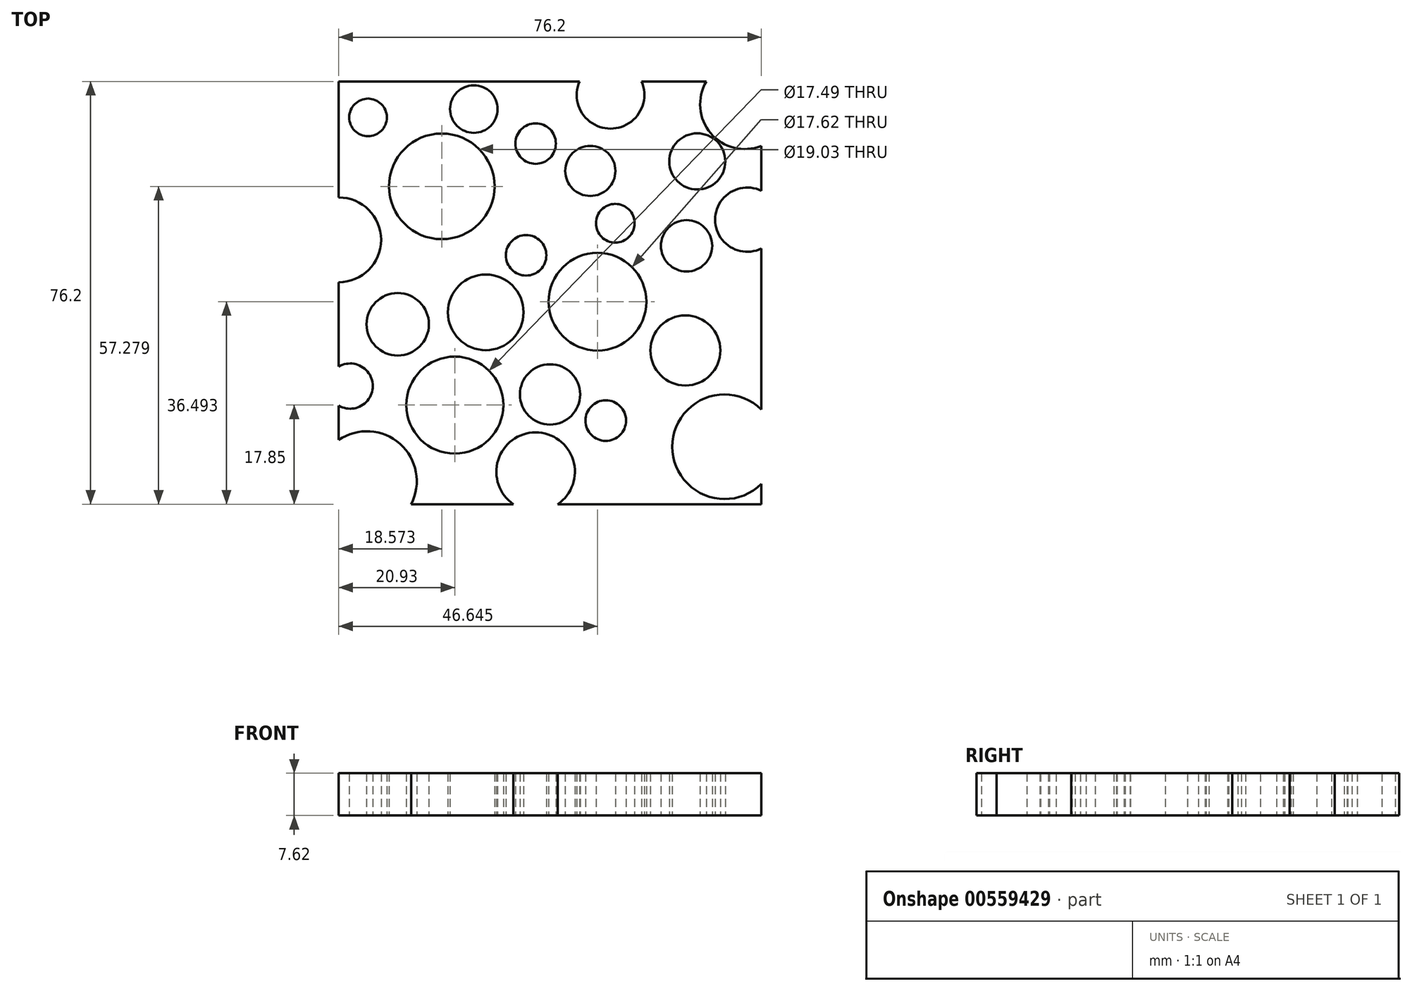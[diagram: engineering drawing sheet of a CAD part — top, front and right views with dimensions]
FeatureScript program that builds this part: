
annotation { "Feature Type Name" : "Feature", "Feature Type Description" : "" }
export const myFeature = defineFeature(function(context is Context, id is Id, definition is map)
    precondition{}
    {
        {
            var Q0;
            Q0=qCreatedBy(makeId("Top.planeOp"),FACE);
            var sketch = newSketch(context, id + "F0", { "sketchPlane" : qUnion([Q0])});
            skLineSegment(sketch, "E0.bottom", {"start": v(38.1, 38.1) * mm, "end": v(-38.1, 38.1) * mm});
            skLineSegment(sketch, "E0.top", {"start": v(38.1, -38.1) * mm, "end": v(-38.1, -38.1) * mm});
            skLineSegment(sketch, "E0.left", {"start": v(38.1, 38.1) * mm, "end": v(38.1, -38.1) * mm});
            skLineSegment(sketch, "E0.right", {"start": v(-38.1, 38.1) * mm, "end": v(-38.1, -38.1) * mm});
            skPoint(sketch, "E0.middle", {"position": v(0, 0) * mm});
            skCircle(sketch, "E1", {"center": v(-19.53, 19.18) * mm, "radius": 9.52 * mm});
            skCircle(sketch, "E2", {"center": v(7.26, 21.96) * mm, "radius": 4.52 * mm});
            skCircle(sketch, "E3", {"center": v(-2.6, 26.9) * mm, "radius": 3.65 * mm});
            skCircle(sketch, "E4", {"center": v(26.54, 23.68) * mm, "radius": 5.06 * mm});
            skCircle(sketch, "E5", {"center": v(8.54, -1.6) * mm, "radius": 8.8 * mm});
            skCircle(sketch, "E6", {"center": v(-4.31, 6.75) * mm, "radius": 3.65 * mm});
            skCircle(sketch, "E7", {"center": v(-27.46, -5.68) * mm, "radius": 5.62 * mm});
            skCircle(sketch, "E8", {"center": v(-17.17, -20.25) * mm, "radius": 8.74 * mm});
            skCircle(sketch, "E9", {"center": v(-11.6, -3.54) * mm, "radius": 6.82 * mm});
            skCircle(sketch, "E10", {"center": v(24.62, 8.46) * mm, "radius": 4.63 * mm});
            skCircle(sketch, "E11", {"center": v(-32.81, 31.6) * mm, "radius": 3.39 * mm});
            skCircle(sketch, "E12", {"center": v(10.9, 35.68) * mm, "radius": 6.1 * mm});
            skCircle(sketch, "E13", {"center": v(31.47, -27.75) * mm, "radius": 9.43 * mm});
            skCircle(sketch, "E14", {"center": v(41.33, -27.54) * mm, "radius": 3.23 * mm});
            skCircle(sketch, "E15", {"center": v(10.04, -23.04) * mm, "radius": 3.66 * mm});
            skCircle(sketch, "E16", {"center": v(24.4, -10.4) * mm, "radius": 6.3 * mm});
            skCircle(sketch, "E17", {"center": v(0, -18.32) * mm, "radius": 5.43 * mm});
            skCircle(sketch, "E18", {"center": v(-2.6, -32.25) * mm, "radius": 7.08 * mm});
            skCircle(sketch, "E19", {"center": v(-33.03, -33.96) * mm, "radius": 9 * mm});
            skCircle(sketch, "E20", {"center": v(-36.03, -16.82) * mm, "radius": 4.08 * mm});
            skCircle(sketch, "E21", {"center": v(-38.1, 9.54) * mm, "radius": 7.64 * mm});
            skCircle(sketch, "E22", {"center": v(-13.74, 33.1) * mm, "radius": 4.3 * mm});
            skCircle(sketch, "E23", {"center": v(35.12, 33.96) * mm, "radius": 8.07 * mm});
            skCircle(sketch, "E24", {"center": v(35.54, 13.18) * mm, "radius": 5.79 * mm});
            skCircle(sketch, "E25", {"center": v(11.76, 12.54) * mm, "radius": 3.49 * mm});
            skSolve(sketch);
        }
        {
            var Q0;
            Q0=makeQuery(id+"F0.imprint","IMPRINT",FACE,{"disambiguationData":[TD([[makeQuery(id+"F0.imprint","IMPRINT",EDGE,{"derivedFrom":sQuery(id+"F0.wireOp",EDGE,"E1")}),-1.0]])]});
            extrude(context, id + "F1", {"entities" : qUnion([Q0]), "depth" : 7.62 * mm, "offsetDistance" : 25.4 * mm});
        }
    });
